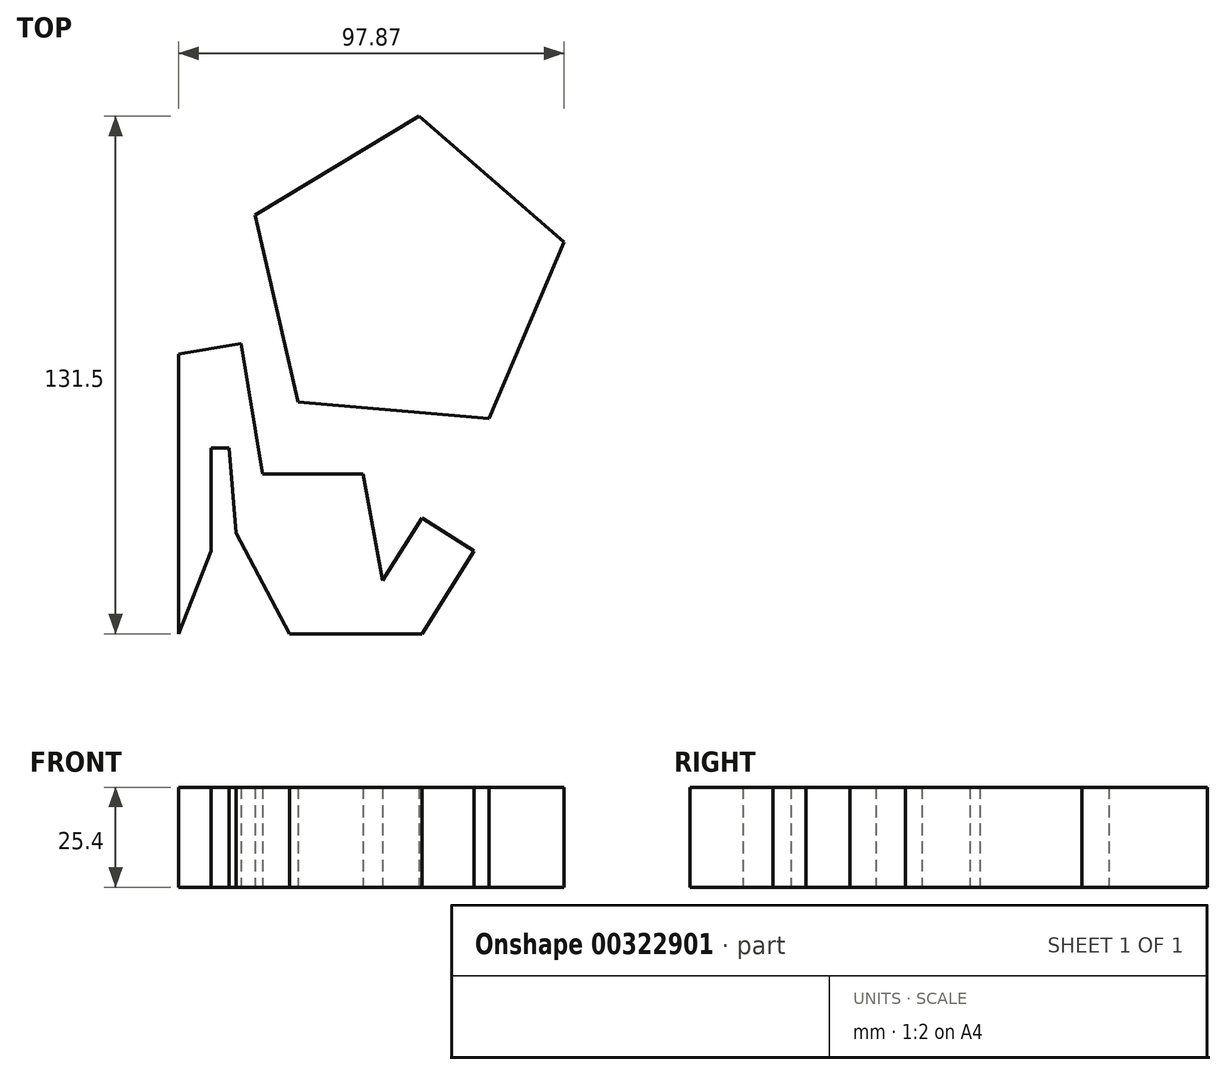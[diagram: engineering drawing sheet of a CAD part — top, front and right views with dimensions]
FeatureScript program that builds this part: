
annotation { "Feature Type Name" : "Feature", "Feature Type Description" : "" }
export const myFeature = defineFeature(function(context is Context, id is Id, definition is map)
    precondition{}
    {
        {
            var Q0;
            Q0=qCreatedBy(makeId("Top.planeOp"),FACE);
            var sketch = newSketch(context, id + "F0", { "sketchPlane" : qUnion([Q0])});
            skCircle(sketch, "E0.cCircle", {"center": v(-9.25, 24.96) * mm, "radius": 41.44 * mm, "construction": true});
            skLineSegment(sketch, "E0.0", {"start": v(12.1, -10.55) * mm, "end": v(-36.42, -6.33) * mm});
            skLineSegment(sketch, "E0.1", {"start": v(-36.42, -6.33) * mm, "end": v(-47.4, 41.13) * mm});
            skLineSegment(sketch, "E0.2", {"start": v(-47.4, 41.13) * mm, "end": v(-5.66, 66.24) * mm});
            skLineSegment(sketch, "E0.3", {"start": v(-5.66, 66.24) * mm, "end": v(31.12, 34.3) * mm});
            skLineSegment(sketch, "E0.4", {"start": v(31.12, 34.3) * mm, "end": v(12.1, -10.55) * mm});
            skLineSegment(sketch, "E1", {"start": v(-47.4, 41.13) * mm, "end": v(21.61, 11.88) * mm});
            skLineSegment(sketch, "E2", {"start": v(-5.66, 66.24) * mm, "end": v(-12.16, -8.44) * mm});
            skLineSegment(sketch, "E3", {"start": v(-36.42, -6.33) * mm, "end": v(12.73, 50.27) * mm});
            skLineSegment(sketch, "E4", {"start": v(31.12, 34.3) * mm, "end": v(-41.91, 17.4) * mm});
            skLineSegment(sketch, "E5", {"start": v(12.1, -10.55) * mm, "end": v(-26.53, 53.69) * mm});
            skSolve(sketch);
        }
        {
            var Q0;
            Q0 = qSketchRegion(id + "F0", true);
            extrude(context, id + "F1", {"entities" : qUnion([Q0]), "depth" : 25.4 * mm});
        }
        {
            var Q0;
            Q0=qCreatedBy(makeId("Top.planeOp"),FACE);
            var sketch = newSketch(context, id + "F2", { "sketchPlane" : qUnion([Q0])});
            skCircle(sketch, "E6", {"center": v(-2.96, 46.77) * mm, "radius": 14.28 * mm});
            skSolve(sketch);
        }
        {
            var Q0;
            Q0=sQuery(id+"F2.wireOp",EDGE,"E6");
            extrude(context, id + "F3", {"bodyType" : ToolBodyType.SURFACE, "surfaceEntities" : qUnion([Q0]), "depth" : 63.75 * mm});
        }
        {
            var Q0;
            Q0=qCreatedBy(makeId("Top.planeOp"),FACE);
            var sketch = newSketch(context, id + "F4", { "sketchPlane" : qUnion([Q0])});
            skLineSegment(sketch, "E7", {"start": v(-52.14, -39.6) * mm, "end": v(-38.56, -65.26) * mm});
            skLineSegment(sketch, "E8", {"start": v(-38.56, -65.26) * mm, "end": v(-4.95, -65.26) * mm});
            skLineSegment(sketch, "E9", {"start": v(-4.95, -65.26) * mm, "end": v(8.32, -44.17) * mm});
            skLineSegment(sketch, "E10", {"start": v(8.32, -44.17) * mm, "end": v(-4.95, -35.82) * mm});
            skLineSegment(sketch, "E11", {"start": v(-4.95, -35.82) * mm, "end": v(-14.95, -51.72) * mm});
            skLineSegment(sketch, "E12", {"start": v(-14.95, -51.72) * mm, "end": v(-19.93, -24.63) * mm});
            skLineSegment(sketch, "E13", {"start": v(-19.93, -24.63) * mm, "end": v(-45.42, -24.63) * mm});
            skLineSegment(sketch, "E14", {"start": v(-45.42, -24.63) * mm, "end": v(-50.86, 8.48) * mm});
            skLineSegment(sketch, "E15", {"start": v(-50.86, 8.48) * mm, "end": v(-66.75, 5.87) * mm});
            skLineSegment(sketch, "E16", {"start": v(-66.75, 5.87) * mm, "end": v(-66.75, -65.26) * mm});
            skLineSegment(sketch, "E17", {"start": v(-66.75, -65.26) * mm, "end": v(-58.49, -44.17) * mm});
            skLineSegment(sketch, "E18", {"start": v(-58.49, -44.17) * mm, "end": v(-58.49, -18) * mm});
            skLineSegment(sketch, "E19", {"start": v(-58.49, -18) * mm, "end": v(-53.95, -18) * mm});
            skLineSegment(sketch, "E20", {"start": v(-53.95, -18) * mm, "end": v(-52.14, -39.6) * mm});
            skSolve(sketch);
        }
        {
            var Q0;
            Q0=makeQuery(id+"F4.imprint","IMPRINT",FACE,{"disambiguationData":[TD([[makeQuery(id+"F4.imprint","IMPRINT",EDGE,{"derivedFrom":sQuery(id+"F4.wireOp",EDGE,"E7")}),1.0]])]});
            extrude(context, id + "F5", {"entities" : qUnion([Q0]), "depth" : 25.4 * mm});
        }
    });
